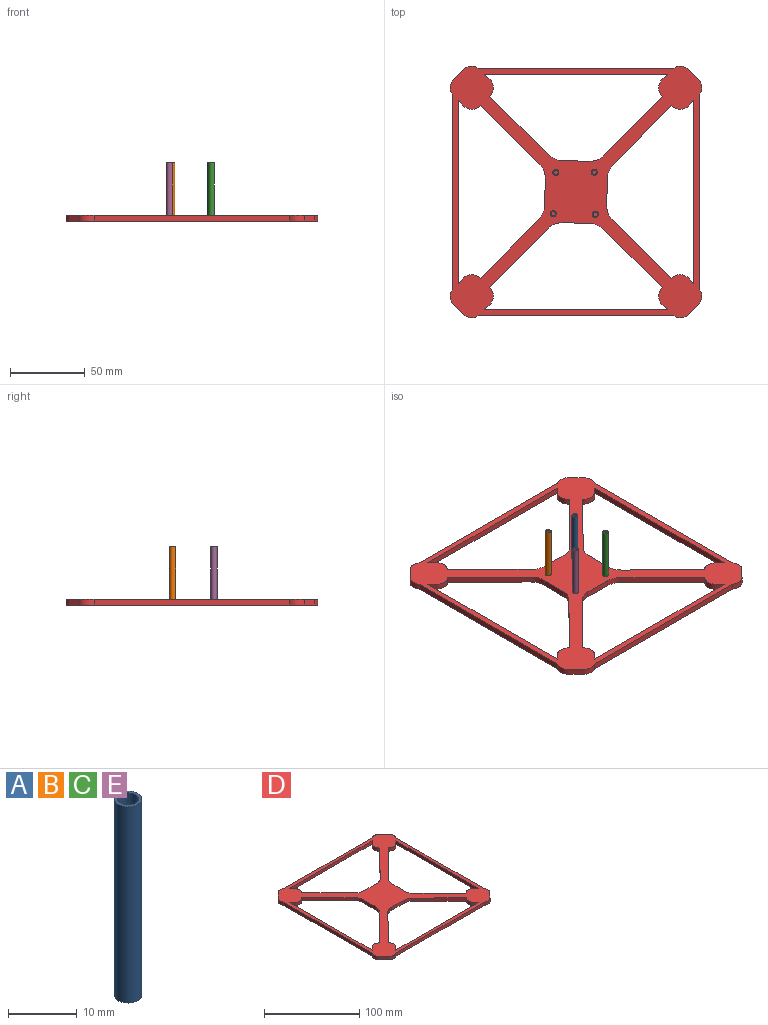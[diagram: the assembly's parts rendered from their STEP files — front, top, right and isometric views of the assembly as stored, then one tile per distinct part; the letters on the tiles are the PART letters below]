
ASSEMBLY  parts=5 mates=4
PART A: 4 faces, bbox 4x4x35 mm
  f0: cylinder r=1.5mm len=35mm, axis (0,0,-1), area 329.9mm2, adj f2,f3
  f1: cylinder r=2mm len=35mm, axis (0,0,-1), area 439.8mm2, adj f2,f3
  f2: plane 4x4mm, normal (0,0,1), area 5.5mm2, adj f0,f1
  f3: plane 4x4mm, normal (0,0,-1), area 5.5mm2, adj f0,f1
PART B: same geometry as A
PART C: same geometry as A
PART D: 66 faces, bbox 168.7x168.7x4 mm
  f0: plane 4x3.94mm, normal (-0.7,-0.71,0), area 22.1mm2, adj f55,f56,f57,f65
  f1: cylinder r=7.62mm len=9.63mm, axis (0,0,-1), area 42mm2, adj f17,f56,f57,f64
  f2: plane 4x3.94mm, normal (-0.71,0.7,0), area 22.1mm2, adj f43,f56,f57,f63
  f3: cylinder r=7.62mm len=9.63mm, axis (0,0,-1), area 42mm2, adj f53,f56,f57,f62
  f4: plane 4x3.94mm, normal (0.7,0.71,0), area 22.1mm2, adj f31,f56,f57,f61
  f5: cylinder r=7.62mm len=9.63mm, axis (0,0,-1), area 42mm2, adj f41,f56,f57,f60
  f6: plane 4x3.94mm, normal (0.71,-0.7,0), area 22.1mm2, adj f19,f56,f57,f59
  f7: cylinder r=7.62mm len=9.63mm, axis (0,0,-1), area 42mm2, adj f29,f56,f57,f58
  f8: plane 4x0.26mm, normal (0.71,-0.7,0), area 1.4mm2, adj f9,f55,f56,f57
  f9: plane 39.73x39.24mm, normal (-0.7,-0.71,0), area 223.4mm2, adj f8,f10,f56,f57
  f10: cylinder r=12.7mm len=9.28mm, axis (0,0,-1), area 41.2mm2, adj f9,f11,f56,f57
  f11: plane 18.53x4mm, normal (-1,0.02,0), area 74.1mm2, adj f10,f12,f56,f57
  f12: cylinder r=12.7mm len=8.68mm, axis (0,0,-1), area 38.6mm2, adj f11,f13,f56,f57
  f13: plane 40x39.52mm, normal (-0.71,0.7,0), area 224.9mm2, adj f12,f14,f56,f57
  f14: plane 4x0.36mm, normal (0.7,0.71,0), area 2mm2, adj f13,f15,f56,f57
  f15: cylinder r=7.62mm len=10.78mm, axis (0,0,-1), area 47.9mm2, adj f14,f16,f56,f57
  f16: plane 4x3.83mm, normal (-0.71,0.7,0), area 21.6mm2, adj f15,f56,f57,f65
  f17: plane 6.94x6.86mm, normal (-0.7,-0.71,0), area 39mm2, adj f1,f18,f56,f57
  f18: cylinder r=7.62mm len=9.57mm, axis (0,0,-1), area 41.6mm2, adj f17,f56,f57,f58
  f19: cylinder r=7.62mm len=10.78mm, axis (0,0,-1), area 47.9mm2, adj f6,f20,f56,f57
  f20: plane 4x0.26mm, normal (0.7,0.71,0), area 1.4mm2, adj f19,f21,f56,f57
  f21: plane 39.73x39.24mm, normal (0.71,-0.7,0), area 223.4mm2, adj f20,f22,f56,f57
  f22: cylinder r=12.7mm len=9.28mm, axis (0,0,-1), area 41.2mm2, adj f21,f23,f56,f57
  f23: plane 18.53x4mm, normal (-0.02,-1,0), area 74.1mm2, adj f22,f24,f56,f57
  f24: cylinder r=12.7mm len=8.68mm, axis (0,0,-1), area 38.6mm2, adj f23,f25,f56,f57
  f25: plane 40x39.52mm, normal (-0.7,-0.71,0), area 224.9mm2, adj f24,f26,f56,f57
  f26: plane 4x0.36mm, normal (-0.71,0.7,0), area 2mm2, adj f25,f27,f56,f57
  f27: cylinder r=7.62mm len=10.78mm, axis (0,0,-1), area 47.9mm2, adj f26,f28,f56,f57
  f28: plane 4x3.83mm, normal (-0.7,-0.71,0), area 21.6mm2, adj f27,f56,f57,f59
  f29: plane 6.94x6.86mm, normal (0.71,-0.7,0), area 39mm2, adj f7,f30,f56,f57
  f30: cylinder r=7.62mm len=9.57mm, axis (0,0,-1), area 41.6mm2, adj f29,f56,f57,f60
  f31: cylinder r=7.62mm len=10.78mm, axis (0,0,-1), area 47.9mm2, adj f4,f32,f56,f57
  f32: plane 4x0.26mm, normal (-0.71,0.7,0), area 1.4mm2, adj f31,f33,f56,f57
  f33: plane 39.73x39.24mm, normal (0.7,0.71,0), area 223.4mm2, adj f32,f34,f56,f57
  f34: cylinder r=12.7mm len=9.28mm, axis (0,0,-1), area 41.2mm2, adj f33,f35,f56,f57
  f35: plane 18.53x4mm, normal (1,-0.02,0), area 74.1mm2, adj f34,f36,f56,f57
  f36: cylinder r=12.7mm len=8.68mm, axis (0,0,-1), area 38.6mm2, adj f35,f37,f56,f57
  f37: plane 40x39.52mm, normal (0.71,-0.7,0), area 224.9mm2, adj f36,f38,f56,f57
  f38: plane 4x0.36mm, normal (-0.7,-0.71,0), area 2mm2, adj f37,f39,f56,f57
  f39: cylinder r=7.62mm len=10.78mm, axis (0,0,-1), area 47.9mm2, adj f38,f40,f56,f57
  f40: plane 4x3.83mm, normal (0.71,-0.7,0), area 21.6mm2, adj f39,f56,f57,f61
  f41: plane 6.94x6.86mm, normal (0.7,0.71,0), area 39mm2, adj f5,f42,f56,f57
  f42: cylinder r=7.62mm len=9.57mm, axis (0,0,-1), area 41.6mm2, adj f41,f56,f57,f62
  f43: cylinder r=7.62mm len=10.78mm, axis (0,0,-1), area 47.9mm2, adj f2,f44,f56,f57
  f44: plane 4x0.26mm, normal (-0.7,-0.71,0), area 1.4mm2, adj f43,f45,f56,f57
  f45: plane 39.73x39.24mm, normal (-0.71,0.7,0), area 223.4mm2, adj f44,f46,f56,f57
  f46: cylinder r=12.7mm len=9.28mm, axis (0,0,-1), area 41.2mm2, adj f45,f47,f56,f57
  f47: plane 18.53x4mm, normal (0.02,1,0), area 74.1mm2, adj f46,f48,f56,f57
  f48: cylinder r=12.7mm len=8.68mm, axis (0,0,-1), area 38.6mm2, adj f47,f49,f56,f57
  f49: plane 40x39.52mm, normal (0.7,0.71,0), area 224.9mm2, adj f48,f50,f56,f57
  f50: plane 4x0.36mm, normal (0.71,-0.7,0), area 2mm2, adj f49,f51,f56,f57
  f51: cylinder r=7.62mm len=10.78mm, axis (0,0,-1), area 47.9mm2, adj f50,f52,f56,f57
  f52: plane 4x3.83mm, normal (0.7,0.71,0), area 21.6mm2, adj f51,f56,f57,f63
  f53: plane 6.94x6.86mm, normal (-0.71,0.7,0), area 39mm2, adj f3,f54,f56,f57
  f54: cylinder r=7.62mm len=9.57mm, axis (0,0,-1), area 41.6mm2, adj f53,f56,f57,f64
  f55: cylinder r=7.62mm len=10.78mm, axis (0,0,-1), area 47.9mm2, adj f0,f8,f56,f57
  f56: plane 168.74x168.74mm, normal (0,0,1), area 8192mm2, adj f0,f1,f2,f3,f4,f5,f6,f7
  f57: plane 168.74x168.74mm, normal (0,0,-1), area 8192mm2, adj f0,f1,f2,f3,f4,f5,f6,f7
  f58: plane 131.28x4mm, normal (0,-1,0), area 525.1mm2, adj f7,f18,f56,f57
  f59: plane 122.85x4mm, normal (0,1,0), area 491.4mm2, adj f6,f28,f56,f57
  f60: plane 131.28x4mm, normal (1,0,0), area 525.1mm2, adj f5,f30,f56,f57
  f61: plane 122.85x4mm, normal (-1,0,0), area 491.4mm2, adj f4,f40,f56,f57
  f62: plane 131.28x4mm, normal (0,1,0), area 525.1mm2, adj f3,f42,f56,f57
  f63: plane 122.85x4mm, normal (0,-1,0), area 491.4mm2, adj f2,f52,f56,f57
  f64: plane 131.28x4mm, normal (-1,0,0), area 525.1mm2, adj f1,f54,f56,f57
  f65: plane 122.85x4mm, normal (1,0,0), area 491.4mm2, adj f0,f16,f56,f57
PART E: same geometry as A
PLACE A t=(-10.48,32.77,8.65)mm
PLACE B t=(-36.23,32.48,8.65)mm
PLACE C t=(-9.74,4.44,8.65)mm
PLACE D t=(-22.75,19.49,4.65)mm
PLACE E t=(-37.97,4.87,8.65)mm
MATE planar B.f1 <-> D.f56  axis (0,0,-1) through (-36.23,32.48,8.65)mm
MATE planar D.f56 <-> A.f1  axis (0,0,1) through (-22.75,19.49,8.65)mm
MATE planar D.f56 <-> C.f1  axis (0,0,1) through (-22.75,19.49,8.65)mm
MATE planar D.f56 <-> E.f1  axis (0,0,1) through (-22.75,19.49,8.65)mm
